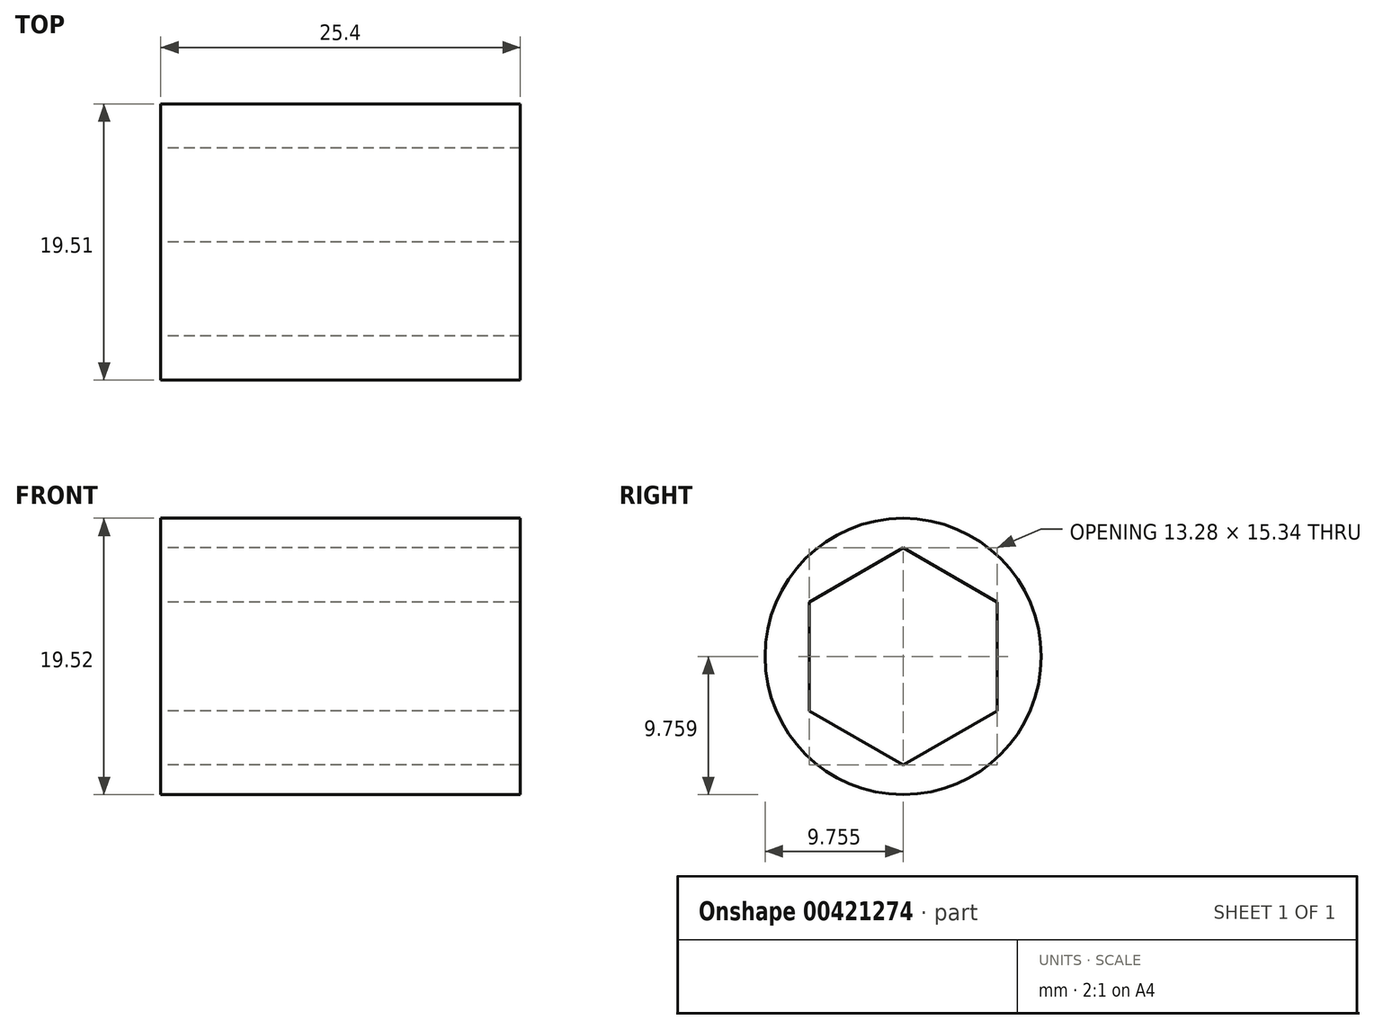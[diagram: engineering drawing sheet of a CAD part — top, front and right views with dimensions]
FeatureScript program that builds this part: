
annotation { "Feature Type Name" : "Feature", "Feature Type Description" : "" }
export const myFeature = defineFeature(function(context is Context, id is Id, definition is map)
    precondition{}
    {
        {
            var Q0;
            Q0=qCreatedBy(makeId("Right.planeOp"),FACE);
            var sketch = newSketch(context, id + "F0", { "sketchPlane" : qUnion([Q0])});
            skCircle(sketch, "E0.cCircle", {"center": v(-0.42, 0.72) * mm, "radius": 6.64 * mm, "construction": true});
            skLineSegment(sketch, "E0.0", {"start": v(6.23, -3.12) * mm, "end": v(-0.42, -6.95) * mm});
            skLineSegment(sketch, "E0.1", {"start": v(-0.42, -6.95) * mm, "end": v(-7.06, -3.12) * mm});
            skLineSegment(sketch, "E0.2", {"start": v(-7.06, -3.12) * mm, "end": v(-7.06, 4.55) * mm});
            skLineSegment(sketch, "E0.3", {"start": v(-7.06, 4.55) * mm, "end": v(-0.42, 8.39) * mm});
            skLineSegment(sketch, "E0.4", {"start": v(-0.42, 8.39) * mm, "end": v(6.23, 4.55) * mm});
            skLineSegment(sketch, "E0.5", {"start": v(6.23, 4.55) * mm, "end": v(6.23, -3.12) * mm});
            skPoint(sketch, "E0.0.midPoint", {"position": v(2.9, -5.03) * mm});
            skCircle(sketch, "E1", {"center": v(-0.42, 0.72) * mm, "radius": 9.76 * mm});
            skSolve(sketch);
        }
        {
            var Q0;
            Q0 = qSketchRegion(id + "F0", true);
            extrude(context, id + "F1", {"entities" : qUnion([Q0]), "depth" : 25.4 * mm});
        }
    });
